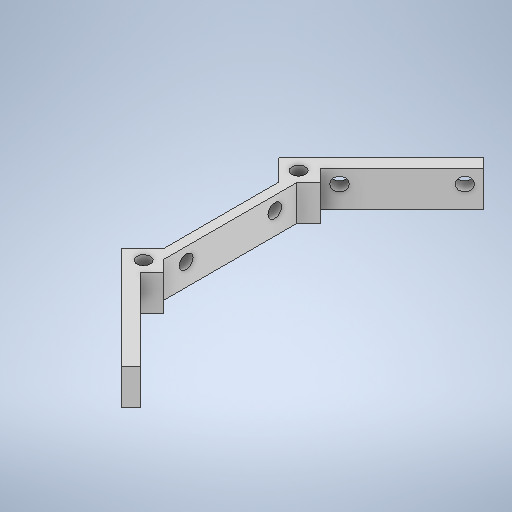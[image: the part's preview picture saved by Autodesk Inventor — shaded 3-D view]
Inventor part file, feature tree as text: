
AUTODESK INVENTOR PART (.ipt)
format: ipt  version: 2025 (Build 290162000, 162)  size: 323,584 bytes
history: native  units: in
note: dims shown in document units (in); Inventor stores cm internally (conversion verified against a paired STEP export)
features: sketch x5, extrude x4
ambient origin geometry x8: Origin, YZ Plane, XZ Plane, XY Plane, X Axis, Y Axis, Z Axis, Center Point
bodies: Body1 (feature_tree)
feature tree (9):
  extrude  "Extrusion2"  Depth=0.9843in
  sketch  "Sketch3"  dims[d8=0.5118in d9=1.0236in]
  extrude  "Extrusion3"  Depth=1.0236in
  extrude  "Extrusion4"  Depth=0.1181in
  extrude  "Extrusion5"  Depth=1.0236in
  sketch  "Sketch1"  dims[d3=0.9843in d6=0.9843in]
  sketch  "Sketch4"  dims[d10=0.1181in d12=0.1201in]
  sketch  "Sketch5"  dims[d13=0.1201in d16=1.0236in]
  sketch  "Sketch6"  dims[d17=135.0deg d18=0.315in d19=0.0in d20=0.1969in d21=0.3937in d22=0.7874in d23=0.122in d24=0.122in d25=0.315in d26=0.0in d27=0.1969in d28=0.3937in d29=0.7874in d30=0.122in d31=0.122in d32=0.315in d33=0.0in d34=1.0236in d35=0.5118in d36=0.1969in d37=0.3937in d38=0.7874in d39=0.122in d40=0.122in d41=0.315in d42=0.0in d14=0.0197in d15=0.0344in]
